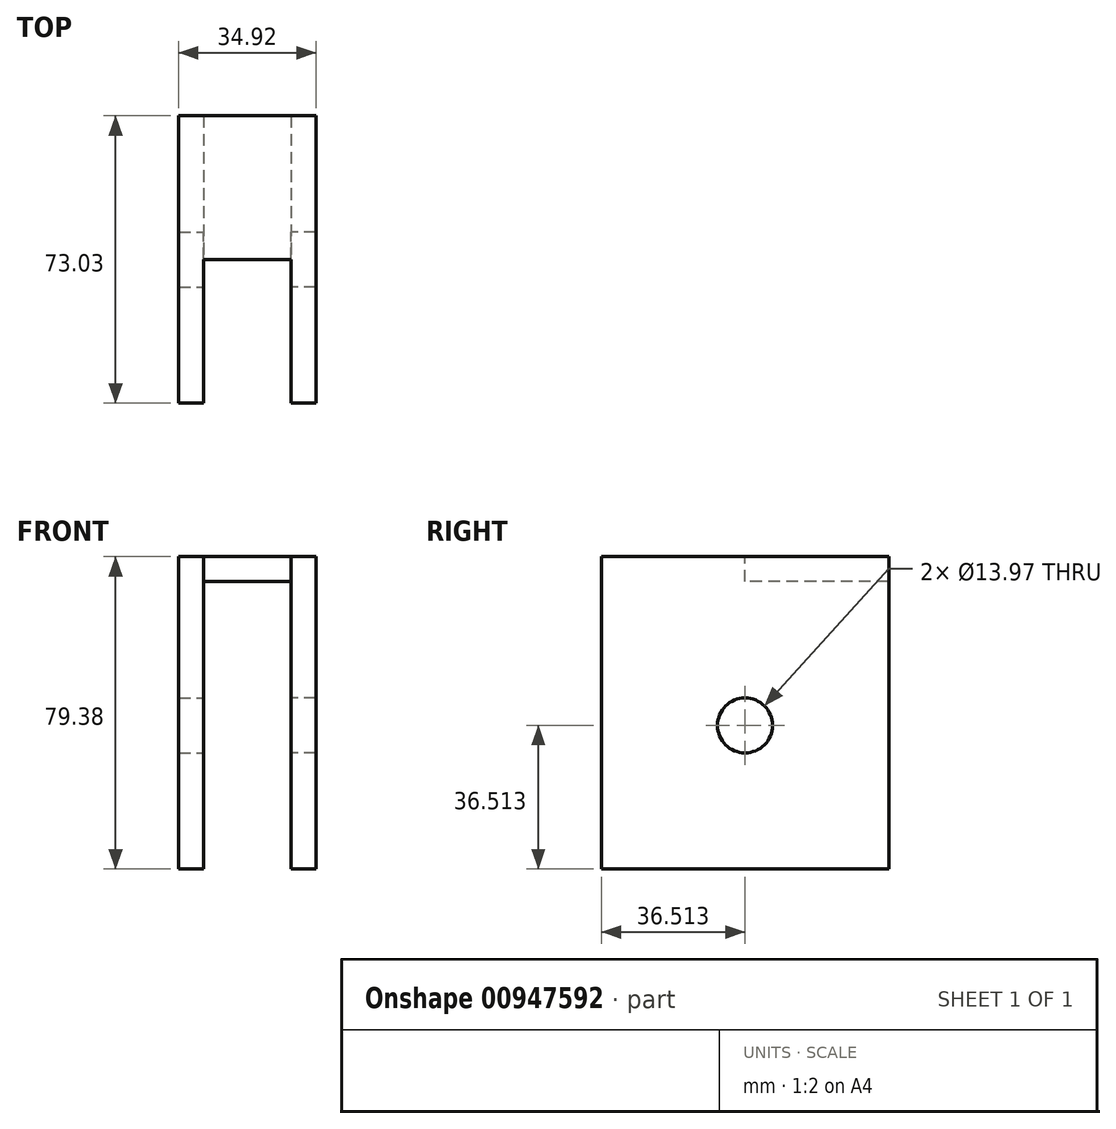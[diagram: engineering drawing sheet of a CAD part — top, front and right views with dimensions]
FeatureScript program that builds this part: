
annotation { "Feature Type Name" : "Feature", "Feature Type Description" : "" }
export const myFeature = defineFeature(function(context is Context, id is Id, definition is map)
    precondition{}
    {
        {
            var Q0;
            Q0=qCreatedBy(makeId("Front.planeOp"),FACE);
            var sketch = newSketch(context, id + "F0", { "sketchPlane" : qUnion([Q0])});
            skLineSegment(sketch, "E0.bottom", {"start": v(-11.11, 0) * mm, "end": v(-17.46, 0) * mm});
            skLineSegment(sketch, "E0.top", {"start": v(0, 79.38) * mm, "end": v(-17.46, 79.38) * mm});
            skLineSegment(sketch, "E0.left", {"start": v(0, 73.03) * mm, "end": v(0, 79.38) * mm});
            skLineSegment(sketch, "E0.right", {"start": v(-17.46, 0) * mm, "end": v(-17.46, 79.38) * mm});
            skLineSegment(sketch, "E1.top", {"start": v(0, 73.03) * mm, "end": v(-11.11, 73.03) * mm});
            skLineSegment(sketch, "E1.right", {"start": v(-11.11, 0) * mm, "end": v(-11.11, 73.03) * mm});
            skSolve(sketch);
        }
        {
            var Q0;
            Q0 = qSketchRegion(id + "F0", true);
            extrude(context, id + "F1", {"entities" : qUnion([Q0]), "oppositeDirection" : true, "depth" : 73.02 * mm, "offsetDistance" : 25.4 * mm});
        }
        {
            var Q0;
            Q0=makeQuery(id+"F1.opExtrude","SWEPT_FACE",FACE,{"disambiguationData":[OSD([sQuery(id+"F0.wireOp",EDGE,"E1.right")])]});
            var sketch = newSketch(context, id + "F2", { "sketchPlane" : qUnion([Q0])});
            skCircle(sketch, "E2", {"center": v(36.51, 36.51) * mm, "radius": 6.99 * mm});
            skSolve(sketch);
        }
        {
            var Q0;
            Q0 = qSketchRegion(id + "F2", true);
            extrude(context, id + "F3", {"entities" : qUnion([Q0]), "operationType" : NewBodyOperationType.REMOVE, "oppositeDirection" : true, "depth" : 25.4 * mm, "offsetDistance" : 25.4 * mm});
        }
        {
            var Q0;
            Q0=makeQuery(id+"F1.opExtrude","SWEPT_BODY",BODY,{"disambiguationData":[OSD([sQuery(id+"F0.wireOp",EDGE,"E0.bottom"),sQuery(id+"F0.wireOp",EDGE,"E0.top"),sQuery(id+"F0.wireOp",EDGE,"E0.left"),sQuery(id+"F0.wireOp",EDGE,"E0.right"),sQuery(id+"F0.wireOp",EDGE,"E1.top"),sQuery(id+"F0.wireOp",EDGE,"E1.right")])]});
            var Q1;
            Q1=qCreatedBy(makeId("Right.planeOp"),FACE);
            mirror(context, id + "F4", {"operationType" : NewBodyOperationType.ADD, "entities" : qUnion([Q0]), "mirrorPlane" : qUnion([Q1])});
        }
        {
            var Q0;
            {var subQ0=makeQuery(id+"F1.opExtrude","SWEPT_FACE",FACE,{"disambiguationData":[OSD([sQuery(id+"F0.wireOp",EDGE,"E0.top")])]});Q0=makeQuery(id+"F4.boolean.opBoolean","MERGE",FACE,{"derivedFrom":[subQ0,makeQuery(id+"F4.opPattern","COPY",FACE,{"derivedFrom":subQ0,"instanceName":"1"})]});}
            var sketch = newSketch(context, id + "F5", { "sketchPlane" : qUnion([Q0])});
            skLineSegment(sketch, "E3.bottom", {"start": v(-11.11, 0) * mm, "end": v(11.11, 0) * mm});
            skLineSegment(sketch, "E3.top", {"start": v(-11.11, 36.51) * mm, "end": v(11.11, 36.51) * mm});
            skLineSegment(sketch, "E3.left", {"start": v(-11.11, 0) * mm, "end": v(-11.11, 36.51) * mm});
            skLineSegment(sketch, "E3.right", {"start": v(11.11, 0) * mm, "end": v(11.11, 36.51) * mm});
            skSolve(sketch);
        }
        {
            var Q0;
            Q0 = qSketchRegion(id + "F5", true);
            extrude(context, id + "F6", {"entities" : qUnion([Q0]), "operationType" : NewBodyOperationType.REMOVE, "oppositeDirection" : true, "depth" : 25.4 * mm, "offsetDistance" : 25.4 * mm});
        }
    });
